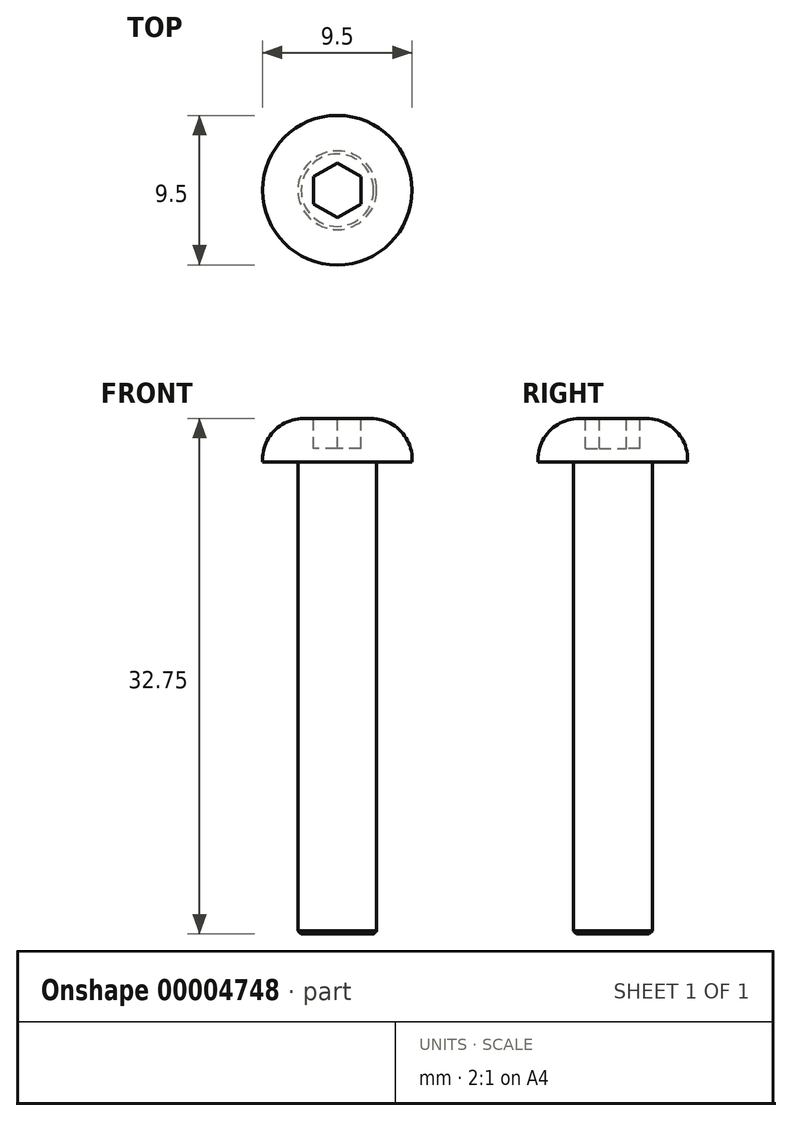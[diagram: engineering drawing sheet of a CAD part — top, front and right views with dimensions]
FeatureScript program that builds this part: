
annotation { "Feature Type Name" : "Feature", "Feature Type Description" : "" }
export const myFeature = defineFeature(function(context is Context, id is Id, definition is map)
    precondition{}
    {
        {
            var Q0;
            Q0=qCreatedBy(makeId("Top.planeOp"),FACE);
            var sketch = newSketch(context, id + "F0", { "sketchPlane" : qUnion([Q0])});
            skCircle(sketch, "E0", {"center": v(0, 0) * mm, "radius": 2.5 * mm});
            skSolve(sketch);
        }
        {
            var Q0;
            Q0 = qSketchRegion(id + "F0", true);
            extrude(context, id + "F1", {"entities" : qUnion([Q0]), "oppositeDirection" : true, "depth" : 30 * mm});
        }
        {
            var Q0;
            Q0=makeQuery(id+"F1.opExtrude","CAP_EDGE",EDGE,{"disambiguationData":[OSD([sQuery(id+"F0.wireOp",EDGE,"E0")])],"isStart":false});
            chamfer(context, id + "F2", {"entities" : qUnion([Q0]), "chamferType" : ChamferType.OFFSET_ANGLE, "width" : 0.2 * mm, "oppositeDirection" : false, "angle" : 45 * degree, "tangentPropagation" : true});
        }
        {
            var Q0;
            Q0=makeQuery(id+"F1.opExtrude","CAP_FACE",FACE,{"disambiguationData":[OSD([sQuery(id+"F0.wireOp",EDGE,"E0")])],"isStart":true});
            var sketch = newSketch(context, id + "F3", { "sketchPlane" : qUnion([Q0])});
            skCircle(sketch, "E1", {"center": v(0, 0) * mm, "radius": 4.75 * mm});
            skSolve(sketch);
        }
        {
            var Q0;
            Q0 = qSketchRegion(id + "F3", true);
            extrude(context, id + "F4", {"entities" : qUnion([Q0]), "operationType" : NewBodyOperationType.ADD, "depth" : 2.75 * mm});
        }
        {
            var Q0;
            Q0=makeQuery(id+"F4.opExtrude","CAP_FACE",FACE,{"disambiguationData":[OSD([sQuery(id+"F3.wireOp",EDGE,"E1")])],"isStart":false});
            var sketch = newSketch(context, id + "F5", { "sketchPlane" : qUnion([Q0])});
            skCircle(sketch, "E2.cCircle", {"center": v(0, 0) * mm, "radius": 1.5 * mm, "construction": true});
            skLineSegment(sketch, "E2.0", {"start": v(-1.5, -0.87) * mm, "end": v(-1.5, 0.87) * mm});
            skLineSegment(sketch, "E2.1", {"start": v(-1.5, 0.87) * mm, "end": v(0, 1.73) * mm});
            skLineSegment(sketch, "E2.2", {"start": v(0, 1.73) * mm, "end": v(1.5, 0.87) * mm});
            skLineSegment(sketch, "E2.3", {"start": v(1.5, 0.87) * mm, "end": v(1.5, -0.87) * mm});
            skLineSegment(sketch, "E2.4", {"start": v(1.5, -0.87) * mm, "end": v(0, -1.73) * mm});
            skLineSegment(sketch, "E2.5", {"start": v(0, -1.73) * mm, "end": v(-1.5, -0.87) * mm});
            skPoint(sketch, "E2.0.midPoint", {"position": v(-1.5, 0) * mm});
            skSolve(sketch);
        }
        {
            var Q0;
            Q0 = qSketchRegion(id + "F5", true);
            extrude(context, id + "F6", {"entities" : qUnion([Q0]), "operationType" : NewBodyOperationType.REMOVE, "oppositeDirection" : true, "depth" : 1.92 * mm});
        }
        {
            var Q0;
            Q0=makeQuery(id+"F4.opExtrude","CAP_EDGE",EDGE,{"disambiguationData":[OSD([sQuery(id+"F3.wireOp",EDGE,"E1")])],"isStart":false});
            fillet(context, id + "F7", {"entities" : qUnion([Q0]), "radius" : (5.2 / 2) * mm, "allowEdgeOverflow" : false});
        }
    });
